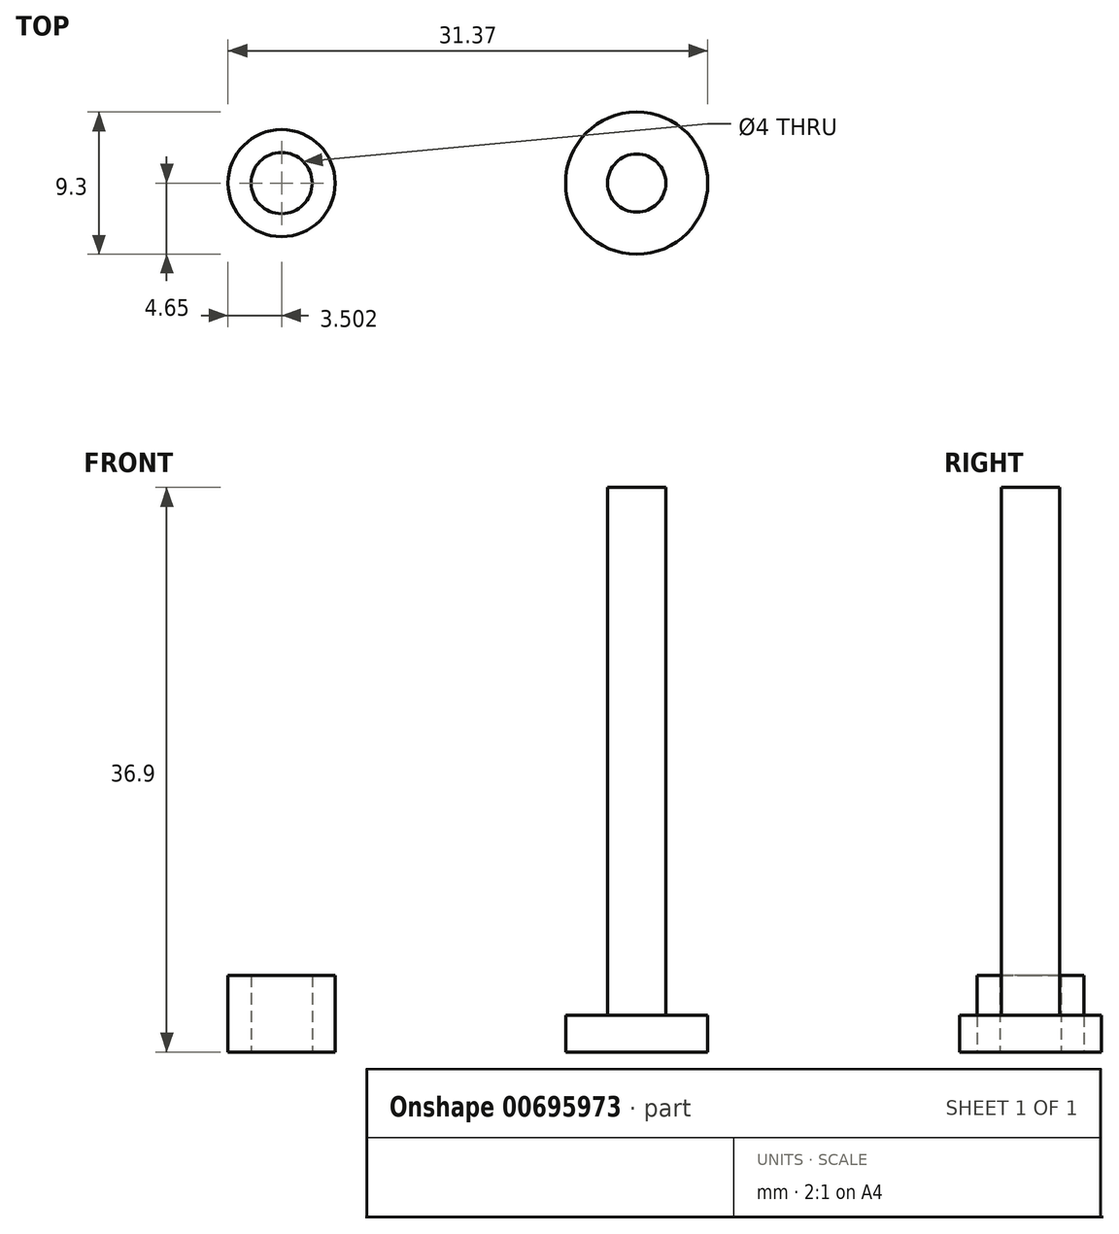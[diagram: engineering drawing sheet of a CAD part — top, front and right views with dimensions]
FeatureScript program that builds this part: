
annotation { "Feature Type Name" : "Feature", "Feature Type Description" : "" }
export const myFeature = defineFeature(function(context is Context, id is Id, definition is map)
    precondition{}
    {
        {
            var Q0;
            Q0=qCreatedBy(makeId("Top.planeOp"),FACE);
            var sketch = newSketch(context, id + "F0", { "sketchPlane" : qUnion([Q0])});
            skCircle(sketch, "E0", {"center": v(0, 0) * mm, "radius": 4.65 * mm});
            skCircle(sketch, "E1", {"center": v(0, 0) * mm, "radius": 1.9 * mm});
            skCircle(sketch, "E2", {"center": v(-23.22, 0) * mm, "radius": 3.5 * mm});
            skCircle(sketch, "E3", {"center": v(-23.22, 0) * mm, "radius": 2 * mm});
            skSolve(sketch);
        }
        {
            var Q0;
            Q0=makeQuery(id+"F0.imprint","IMPRINT",FACE,{"disambiguationData":[TD([[makeQuery(id+"F0.imprint","IMPRINT",EDGE,{"derivedFrom":sQuery(id+"F0.wireOp",EDGE,"E1")}),1.0]])]});
            var Q1;
            Q1=makeQuery(id+"F0.imprint","IMPRINT",FACE,{"disambiguationData":[TD([[makeQuery(id+"F0.imprint","IMPRINT",EDGE,{"derivedFrom":sQuery(id+"F0.wireOp",EDGE,"E0")}),1.0]])]});
            extrude(context, id + "F1", {"entities" : qUnion([Q0, Q1]), "depth" : 2.4 * mm, "offsetDistance" : 25 * mm});
        }
        {
            var Q0;
            Q0=makeQuery(id+"F1.opExtrude","CAP_FACE",FACE,{"disambiguationData":[OSD([sQuery(id+"F0.wireOp",EDGE,"E0")])],"isStart":false});
            var sketch = newSketch(context, id + "F2", { "sketchPlane" : qUnion([Q0])});
            skCircle(sketch, "E4.0", {"center": v(0, 0) * mm, "radius": 1.9 * mm});
            skSolve(sketch);
        }
        {
            var Q0;
            Q0=makeQuery(id+"F2.imprint","IMPRINT",FACE,{"disambiguationData":[TD([[makeQuery(id+"F2.imprint","IMPRINT",EDGE,{"derivedFrom":sQuery(id+"F2.wireOp",EDGE,"E4.0")}),1.0]])]});
            extrude(context, id + "F3", {"entities" : qUnion([Q0]), "operationType" : NewBodyOperationType.ADD, "depth" : 34.5 * mm, "offsetDistance" : 25 * mm});
        }
        {
            var Q0;
            Q0=makeQuery(id+"F0.imprint","IMPRINT",FACE,{"disambiguationData":[TD([[makeQuery(id+"F0.imprint","IMPRINT",EDGE,{"derivedFrom":sQuery(id+"F0.wireOp",EDGE,"E2")}),1.0]])]});
            extrude(context, id + "F4", {"entities" : qUnion([Q0]), "depth" : 5 * mm, "offsetDistance" : 25 * mm});
        }
    });
